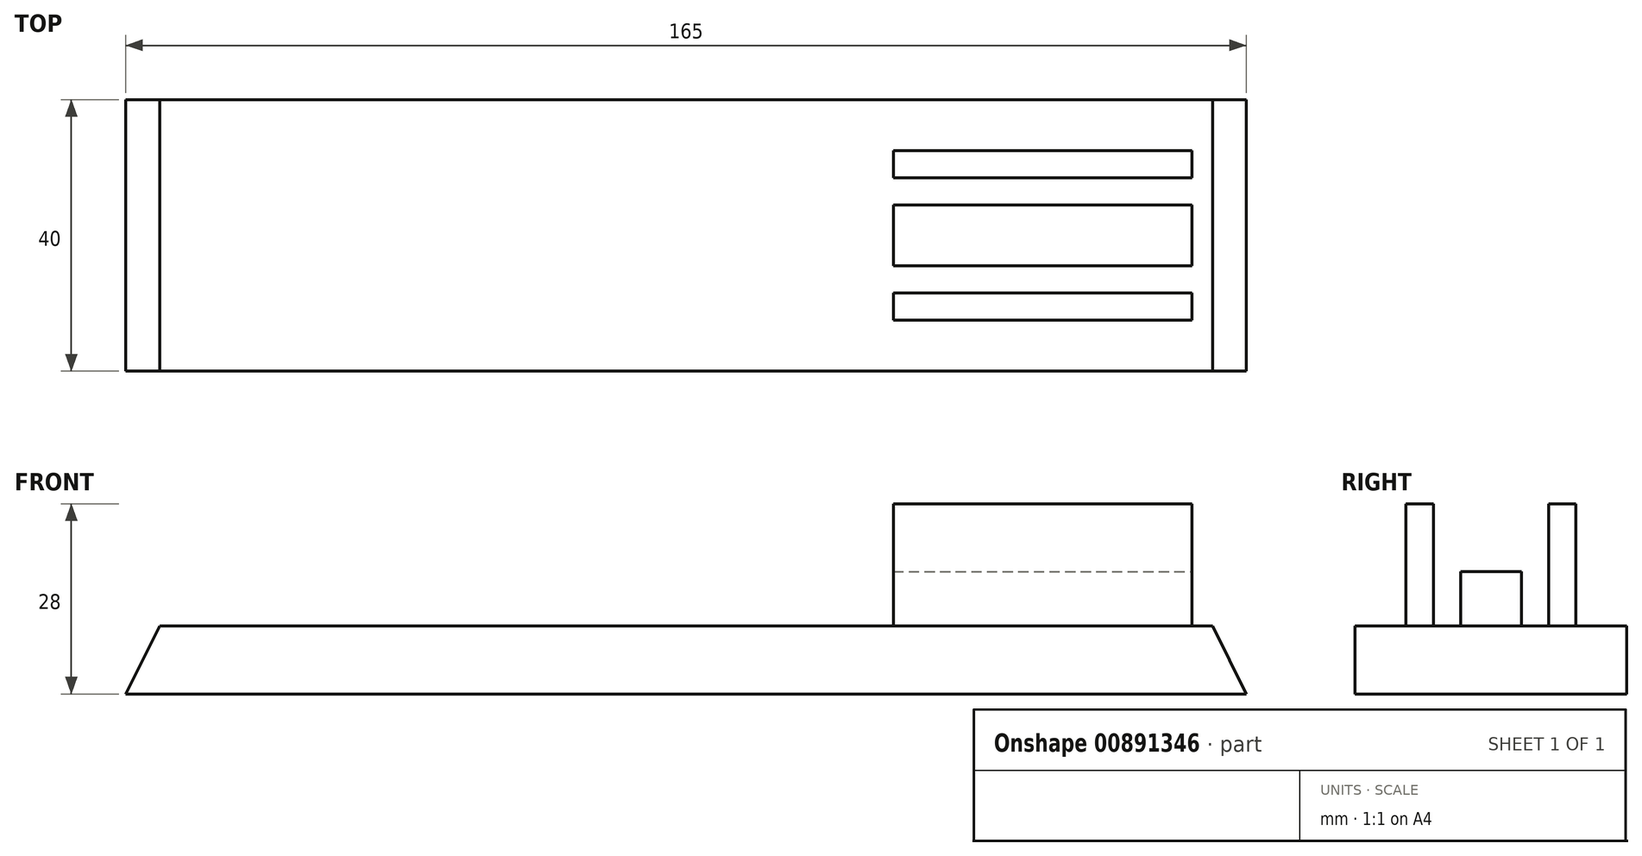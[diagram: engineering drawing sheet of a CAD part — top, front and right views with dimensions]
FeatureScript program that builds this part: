
annotation { "Feature Type Name" : "Feature", "Feature Type Description" : "" }
export const myFeature = defineFeature(function(context is Context, id is Id, definition is map)
    precondition{}
    {
        {
            var Q0;
            Q0=qCreatedBy(makeId("Top.planeOp"),FACE);
            var sketch = newSketch(context, id + "F0", { "sketchPlane" : qUnion([Q0])});
            skLineSegment(sketch, "E0.bottom", {"start": v(0, 0) * mm, "end": v(165, 0) * mm});
            skLineSegment(sketch, "E0.top", {"start": v(0, 40) * mm, "end": v(165, 40) * mm});
            skLineSegment(sketch, "E0.left", {"start": v(0, 0) * mm, "end": v(0, 40) * mm});
            skLineSegment(sketch, "E0.right", {"start": v(165, 0) * mm, "end": v(165, 40) * mm});
            skSolve(sketch);
        }
        {
            var Q0;
            Q0 = qSketchRegion(id + "F0", true);
            extrude(context, id + "F1", {"entities" : qUnion([Q0]), "depth" : 10 * mm, "offsetDistance" : 25 * mm});
        }
        {
            var Q0;
            Q0=makeQuery(id+"F1.opExtrude","CAP_EDGE",EDGE,{"disambiguationData":[OSD([sQuery(id+"F0.wireOp",EDGE,"E0.right")])],"isStart":false});
            chamfer(context, id + "F2", {"entities" : qUnion([Q0]), "chamferType" : ChamferType.TWO_OFFSETS, "width1" : 5 * mm, "oppositeDirection" : false, "width2" : 10 * mm, "tangentPropagation" : true});
        }
        {
            var Q0;
            Q0=makeQuery(id+"F1.opExtrude","CAP_EDGE",EDGE,{"disambiguationData":[OSD([sQuery(id+"F0.wireOp",EDGE,"E0.left")])],"isStart":false});
            chamfer(context, id + "F3", {"entities" : qUnion([Q0]), "chamferType" : ChamferType.TWO_OFFSETS, "width1" : 10 * mm, "oppositeDirection" : false, "width2" : 5 * mm, "tangentPropagation" : true});
        }
        {
            var Q0;
            Q0=makeQuery(id+"F1.opExtrude","CAP_FACE",FACE,{"disambiguationData":[OSD([sQuery(id+"F0.wireOp",EDGE,"E0.bottom"),sQuery(id+"F0.wireOp",EDGE,"E0.top"),sQuery(id+"F0.wireOp",EDGE,"E0.left"),sQuery(id+"F0.wireOp",EDGE,"E0.right")])],"isStart":false});
            var sketch = newSketch(context, id + "F4", { "sketchPlane" : qUnion([Q0])});
            skLineSegment(sketch, "E1.bottom", {"start": v(113, 32.5) * mm, "end": v(157, 32.5) * mm});
            skLineSegment(sketch, "E1.top", {"start": v(113, 7.5) * mm, "end": v(157, 7.5) * mm});
            skLineSegment(sketch, "E1.left", {"start": v(113, 32.5) * mm, "end": v(113, 7.5) * mm});
            skLineSegment(sketch, "E1.right", {"start": v(157, 32.5) * mm, "end": v(157, 7.5) * mm});
            skLineSegment(sketch, "E2.0", {"start": v(113, 28.5) * mm, "end": v(157, 28.5) * mm});
            skLineSegment(sketch, "E3.0", {"start": v(113, 11.5) * mm, "end": v(157, 11.5) * mm});
            skLineSegment(sketch, "E4.0", {"start": v(113, 15.5) * mm, "end": v(157, 15.5) * mm});
            skLineSegment(sketch, "E5.0", {"start": v(113, 24.5) * mm, "end": v(157, 24.5) * mm});
            skSolve(sketch);
        }
        {
            var Q0;
            {var subQ0=sQuery(id+"F4.wireOp",EDGE,"E1.bottom");Q0=makeQuery(id+"F4.imprint","IMPRINT",FACE,{"disambiguationData":[TD([[makeQuery(id+"F4.imprint","IMPRINT",EDGE,{"derivedFrom":subQ0}),-1.0]])]});}
            var Q1;
            {var subQ0=sQuery(id+"F4.wireOp",EDGE,"E1.top");Q1=makeQuery(id+"F4.imprint","IMPRINT",FACE,{"disambiguationData":[TD([[makeQuery(id+"F4.imprint","IMPRINT",EDGE,{"derivedFrom":subQ0}),1.0]])]});}
            extrude(context, id + "F5", {"entities" : qUnion([Q0, Q1]), "operationType" : NewBodyOperationType.ADD, "depth" : 18 * mm, "offsetDistance" : 25 * mm});
        }
        {
            var Q0;
            {var subQ0=sQuery(id+"F4.wireOp",EDGE,"E4.0");Q0=makeQuery(id+"F4.imprint","IMPRINT",FACE,{"disambiguationData":[TD([[makeQuery(id+"F4.imprint","IMPRINT",EDGE,{"derivedFrom":subQ0}),1.0]])]});}
            extrude(context, id + "F6", {"entities" : qUnion([Q0]), "operationType" : NewBodyOperationType.ADD, "depth" : 8 * mm, "offsetDistance" : 25 * mm});
        }
    });
